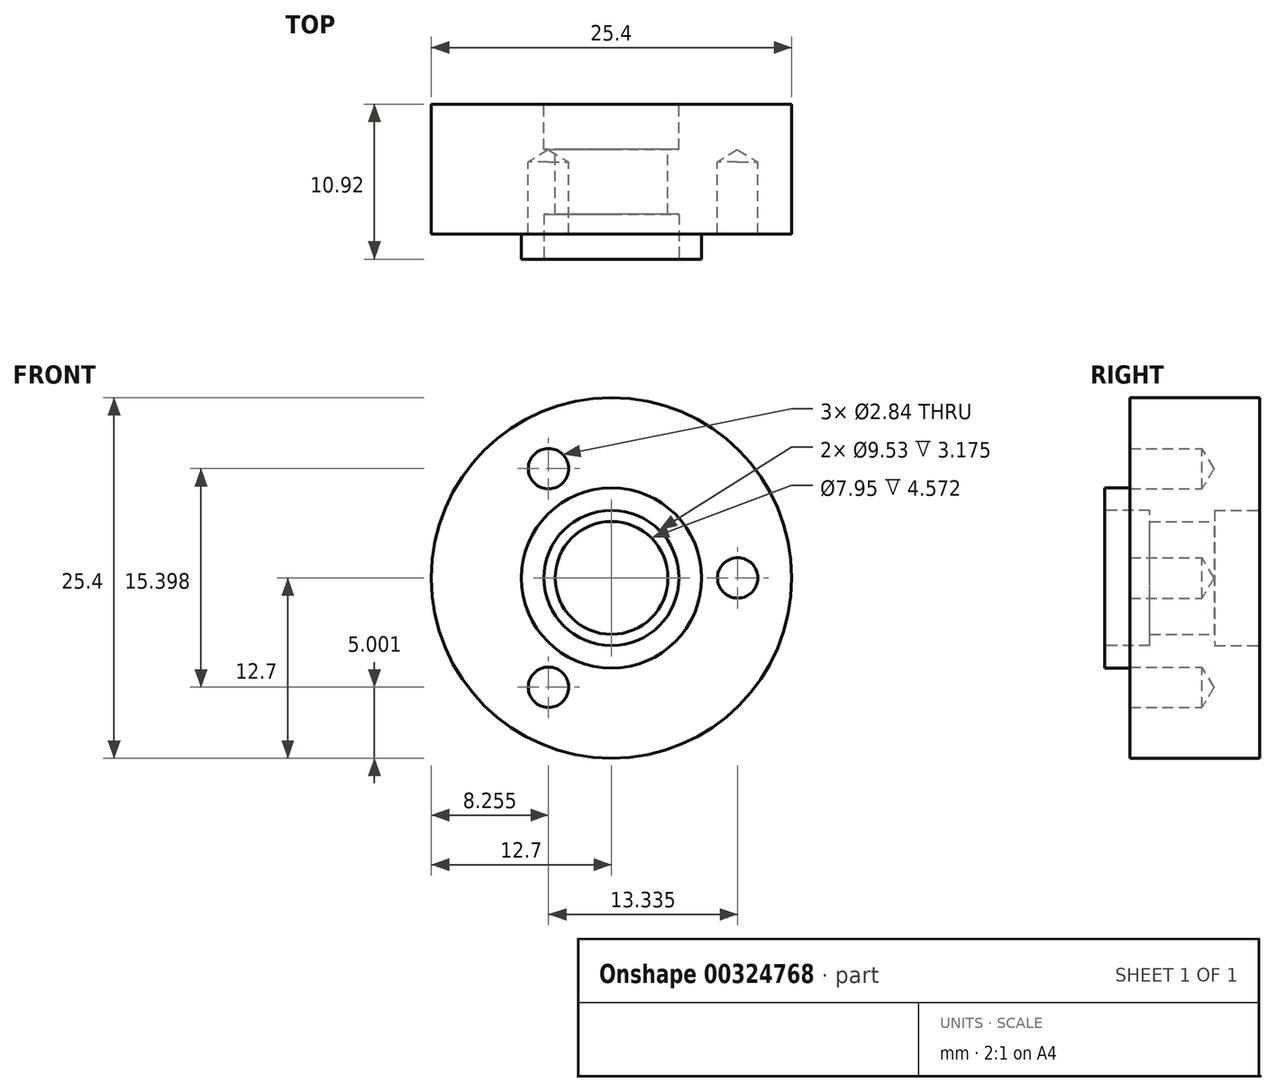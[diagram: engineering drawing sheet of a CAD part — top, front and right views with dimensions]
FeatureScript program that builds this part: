
annotation { "Feature Type Name" : "Feature", "Feature Type Description" : "" }
export const myFeature = defineFeature(function(context is Context, id is Id, definition is map)
    precondition{}
    {
        {
            var Q0;
            Q0=qCreatedBy(makeId("Front.planeOp"),FACE);
            var sketch = newSketch(context, id + "F0", { "sketchPlane" : qUnion([Q0])});
            skCircle(sketch, "E0", {"center": v(0, 0) * mm, "radius": 12.7 * mm});
            skCircle(sketch, "E1", {"center": v(0, 0) * mm, "radius": 3.98 * mm});
            skSolve(sketch);
        }
        {
            var Q0;
            Q0=makeQuery(id+"F0.imprint","IMPRINT",FACE,{"disambiguationData":[TD([[makeQuery(id+"F0.imprint","IMPRINT",EDGE,{"derivedFrom":sQuery(id+"F0.wireOp",EDGE,"E0")}),1.0]])]});
            extrude(context, id + "F1", {"entities" : qUnion([Q0]), "depth" : 9.14 * mm, "offsetDistance" : 25.4 * mm});
        }
        {
            var Q0;
            Q0=makeQuery(id+"F1.opExtrude","CAP_FACE",FACE,{"disambiguationData":[OSD([sQuery(id+"F0.wireOp",EDGE,"E0"),sQuery(id+"F0.wireOp",EDGE,"E1")])],"isStart":false});
            var sketch = newSketch(context, id + "F2", { "sketchPlane" : qUnion([Q0])});
            skCircle(sketch, "E2", {"center": v(0, 0) * mm, "radius": 6.35 * mm});
            skSolve(sketch);
        }
        {
            var Q0;
            Q0=makeQuery(id+"F2.imprint","IMPRINT",FACE,{"disambiguationData":[TD([[makeQuery(id+"F2.imprint","IMPRINT",EDGE,{"derivedFrom":sQuery(id+"F2.wireOp",EDGE,"E2")}),1.0]])]});
            extrude(context, id + "F3", {"entities" : qUnion([Q0]), "operationType" : NewBodyOperationType.ADD, "depth" : 1.78 * mm, "offsetDistance" : 25.4 * mm});
        }
        {
            var Q0;
            Q0=makeQuery(id+"F3.opExtrude","CAP_FACE",FACE,{"disambiguationData":[OSD([sQuery(id+"F0.wireOp",EDGE,"E1"),sQuery(id+"F2.wireOp",EDGE,"E2")])],"isStart":false});
            var sketch = newSketch(context, id + "F4", { "sketchPlane" : qUnion([Q0])});
            skCircle(sketch, "E3", {"center": v(0, 0) * mm, "radius": 4.76 * mm});
            skCircle(sketch, "E4", {"center": v(0, 0) * mm, "radius": 3.18 * mm});
            skSolve(sketch);
        }
        {
            var Q0;
            Q0=makeQuery(id+"F4.imprint","IMPRINT",FACE,{"disambiguationData":[TD([[makeQuery(id+"F4.imprint","IMPRINT",EDGE,{"derivedFrom":sQuery(id+"F4.wireOp",EDGE,"E3")}),1.0]])]});
            extrude(context, id + "F5", {"entities" : qUnion([Q0]), "operationType" : NewBodyOperationType.REMOVE, "oppositeDirection" : true, "depth" : 3.17 * mm, "offsetDistance" : 25.4 * mm});
        }
        {
            var Q0;
            Q0=makeQuery(id+"F1.opExtrude","CAP_FACE",FACE,{"disambiguationData":[OSD([sQuery(id+"F0.wireOp",EDGE,"E0"),sQuery(id+"F0.wireOp",EDGE,"E1")])],"isStart":true});
            var sketch = newSketch(context, id + "F6", { "sketchPlane" : qUnion([Q0])});
            skCircle(sketch, "E5", {"center": v(0, 0) * mm, "radius": 3.18 * mm});
            skCircle(sketch, "E6", {"center": v(0, 0) * mm, "radius": 4.76 * mm});
            skSolve(sketch);
        }
        {
            var Q0;
            Q0=makeQuery(id+"F6.imprint","IMPRINT",FACE,{"disambiguationData":[TD([[makeQuery(id+"F6.imprint","IMPRINT",EDGE,{"derivedFrom":sQuery(id+"F6.wireOp",EDGE,"E6")}),1.0]])]});
            extrude(context, id + "F7", {"entities" : qUnion([Q0]), "operationType" : NewBodyOperationType.REMOVE, "oppositeDirection" : true, "depth" : 3.17 * mm, "offsetDistance" : 25.4 * mm});
        }
        {
            var Q0;
            Q0=makeQuery(id+"F1.opExtrude","CAP_FACE",FACE,{"disambiguationData":[OSD([sQuery(id+"F0.wireOp",EDGE,"E0"),sQuery(id+"F0.wireOp",EDGE,"E1")])],"isStart":false});
            var sketch = newSketch(context, id + "F8", { "sketchPlane" : qUnion([Q0])});
            skPoint(sketch, "E7", {"position": v(8.9, 0) * mm});
            skPoint(sketch, "E8.1.0", {"position": v(-4.44, 7.7) * mm});
            skPoint(sketch, "E8.2.0", {"position": v(-4.45, -7.7) * mm});
            skPoint(sketch, "E8.center", {"position": v(0, 0) * mm});
            skSolve(sketch);
        }
        {
            var Q0;
            Q0=sQuery(id+"F8.wireOp",VERTEX,"E7");
            var Q1;
            Q1=sQuery(id+"F8.wireOp",VERTEX,"E8.1.0");
            var Q2;
            Q2=sQuery(id+"F8.wireOp",VERTEX,"E8.2.0");
            var Q3;
            Q3=makeQuery(id+"F1.opExtrude","SWEPT_BODY",BODY,{"disambiguationData":[OSD([sQuery(id+"F0.wireOp",EDGE,"E0"),sQuery(id+"F0.wireOp",EDGE,"E1")])]});
            hole(context, id + "F9", {"style" : HoleStyle.SIMPLE, "endStyle" : HoleEndStyle.BLIND, "holeDiameter" : 2.84 * mm, "majorDiameter" : 6.35 * mm, "holeDepth" : 5.08 * mm, "tappedDepth" : 12.7 * mm, "tapClearance" : 3, "locations" : qUnion([Q0, Q1, Q2]), "scope" : qUnion([Q3])});
        }
    });
